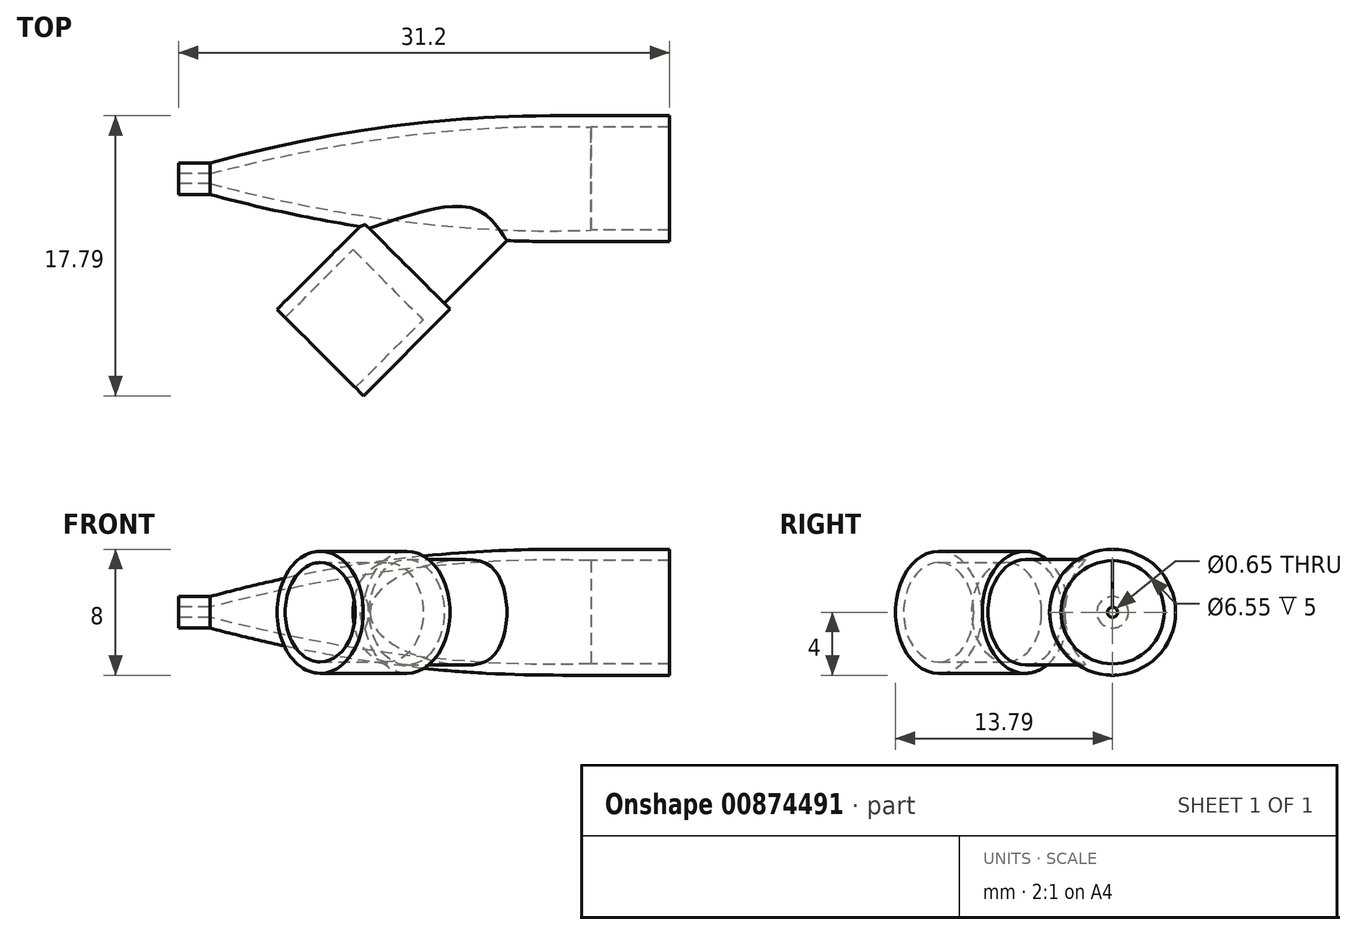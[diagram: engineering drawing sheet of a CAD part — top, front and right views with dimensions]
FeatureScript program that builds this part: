
annotation { "Feature Type Name" : "Feature", "Feature Type Description" : "" }
export const myFeature = defineFeature(function(context is Context, id is Id, definition is map)
    precondition{}
    {
        {
            var Q0;
            Q0=qCreatedBy(makeId("Front.planeOp"),FACE);
            var sketch = newSketch(context, id + "F0", { "sketchPlane" : qUnion([Q0])});
            skLineSegment(sketch, "E0.bottom", {"start": v(1, 1) * mm, "end": v(-1, 1) * mm});
            skLineSegment(sketch, "E0.top", {"start": v(1, 0.33) * mm, "end": v(-1, 0.33) * mm});
            skLineSegment(sketch, "E0.left", {"start": v(1, 1) * mm, "end": v(1, 0.33) * mm});
            skLineSegment(sketch, "E0.right", {"start": v(-1, 1) * mm, "end": v(-1, 0.32) * mm});
            skLineSegment(sketch, "E1.bottom", {"start": v(1, -0.33) * mm, "end": v(-1, -0.33) * mm, "construction": true});
            skLineSegment(sketch, "E1.top", {"start": v(1, -1) * mm, "end": v(-1, -1) * mm, "construction": true});
            skLineSegment(sketch, "E1.left", {"start": v(1, -0.33) * mm, "end": v(1, -1) * mm, "construction": true});
            skLineSegment(sketch, "E1.right", {"start": v(-1, -0.33) * mm, "end": v(-1, -1) * mm, "construction": true});
            skLineSegment(sketch, "E2", {"start": v(0, 0.33) * mm, "end": v(0, -0.33) * mm, "construction": true});
            skLineSegment(sketch, "E3.bottom", {"start": v(30.2, 3.28) * mm, "end": v(25.2, 3.28) * mm});
            skLineSegment(sketch, "E3.top", {"start": v(30.2, -4.73) * mm, "end": v(25.2, -4.72) * mm, "construction": true});
            skLineSegment(sketch, "E3.left", {"start": v(30.2, 4) * mm, "end": v(30.2, 3.28) * mm});
            skLineSegment(sketch, "E3.right", {"start": v(25.2, 4) * mm, "end": v(25.2, 3.28) * mm});
            skLineSegment(sketch, "E4.bottom", {"start": v(30.2, -4) * mm, "end": v(25.2, -4) * mm, "construction": true});
            skLineSegment(sketch, "E4.top", {"start": v(30.2, 4) * mm, "end": v(25.2, 4) * mm});
            skLineSegment(sketch, "E5.trimOffspring", {"start": v(25.2, -4) * mm, "end": v(25.2, -4.72) * mm, "construction": true});
            skLineSegment(sketch, "E6.trimOffspring", {"start": v(30.2, -4) * mm, "end": v(30.2, -4.72) * mm, "construction": true});
            skLineSegment(sketch, "E7", {"start": v(27.7, 4) * mm, "end": v(27.7, -4) * mm, "construction": true});
            skLineSegment(sketch, "E8", {"start": v(0, 0) * mm, "end": v(27.7, 0) * mm, "construction": true});
            skFitSpline(sketch, "E9", {"points": [v(25.2, 4) * mm, v(1, 1) * mm], "startDerivative": vector(-15, 0) * mm, "endDerivative": vector(-34.77, -9.32) * mm});
            skFitSpline(sketch, "E10", {"points": [v(25.2, 3.28) * mm, v(1, 0.33) * mm], "startDerivative": vector(-15, 0.45) * mm, "endDerivative": vector(-34.77, -8.93) * mm});
            skLineSegment(sketch, "E11", {"start": v(27.7, 3.28) * mm, "end": v(27.7, 0) * mm});
            skLineSegment(sketch, "E12", {"start": v(27.7, 0) * mm, "end": v(1, 0) * mm});
            skLineSegment(sketch, "E13", {"start": v(1, 0) * mm, "end": v(1, 0.33) * mm});
            skLineSegment(sketch, "E14", {"start": v(1, 1) * mm, "end": v(12.6, 4.1) * mm, "construction": true});
            skLineSegment(sketch, "E15", {"start": v(20.2, 3.28) * mm, "end": v(20.2, 4) * mm, "construction": true});
            skLineSegment(sketch, "E16", {"start": v(12.6, 3.3) * mm, "end": v(12.6, 2.63) * mm, "construction": true});
            skSolve(sketch);
        }
        {
            var Q0;
            Q0=makeQuery(id+"F0.imprint","IMPRINT",FACE,{"disambiguationData":[TD([[makeQuery(id+"F0.imprint","IMPRINT",EDGE,{"derivedFrom":sQuery(id+"F0.wireOp",EDGE,"E0.bottom")}),1.0]])]});
            var Q1;
            Q1=makeQuery(id+"F0.imprint","IMPRINT",FACE,{"disambiguationData":[TD([[makeQuery(id+"F0.imprint","IMPRINT",EDGE,{"derivedFrom":sQuery(id+"F0.wireOp",EDGE,"E0.left")}),1.0]])]});
            var Q2;
            Q2=makeQuery(id+"F0.imprint","IMPRINT",FACE,{"disambiguationData":[TD([[makeQuery(id+"F0.imprint","IMPRINT",EDGE,{"derivedFrom":sQuery(id+"F0.wireOp",EDGE,"E3.bottom")}),-1.0]])]});
            var Q3;
            Q3=sQuery(id+"F0.wireOp",EDGE,"E8");
            revolve(context, id + "F1", {"surfaceOperationType" : NewSurfaceOperationType.NEW, "entities" : qUnion([Q0, Q1, Q2]), "axis" : qUnion([Q3]), "revolveType" : RevolveType.FULL});
        }
        {
            var Q0;
            Q0=qCreatedBy(makeId("Top.planeOp"),FACE);
            var sketch = newSketch(context, id + "F2", { "sketchPlane" : qUnion([Q0])});
            skLineSegment(sketch, "E17", {"start": v(19.05, 0) * mm, "end": v(5.58, -13.47) * mm, "construction": true});
            skLineSegment(sketch, "E18", {"start": v(0, 0) * mm, "end": v(19.05, 0) * mm, "construction": true});
            skLineSegment(sketch, "E19", {"start": v(15.88, -3.18) * mm, "end": v(12.31, -6.74) * mm});
            skLineSegment(sketch, "E20", {"start": v(16.24, -8.29) * mm, "end": v(15.88, -7.92) * mm});
            skLineSegment(sketch, "E21", {"start": v(15.88, -7.92) * mm, "end": v(20.37, -3.43) * mm});
            skLineSegment(sketch, "E22", {"start": v(12.31, -6.74) * mm, "end": v(14.54, -8.96) * mm});
            skLineSegment(sketch, "E23", {"start": v(14.54, -8.96) * mm, "end": v(10.23, -13.28) * mm});
            skLineSegment(sketch, "E24", {"start": v(10.23, -13.28) * mm, "end": v(10.74, -13.79) * mm});
            skLineSegment(sketch, "E25", {"start": v(10.74, -13.79) * mm, "end": v(16.24, -8.29) * mm});
            skLineSegment(sketch, "E26", {"start": v(15.88, -3.18) * mm, "end": v(20.37, -3.43) * mm});
            skSolve(sketch);
        }
        {
            var Q0;
            Q0 = qSketchRegion(id + "F2", true);
            var Q1;
            Q1=sQuery(id+"F2.wireOp",EDGE,"E17");
            revolve(context, id + "F3", {"operationType" : NewBodyOperationType.ADD, "surfaceOperationType" : NewSurfaceOperationType.NEW, "entities" : qUnion([Q0]), "axis" : qUnion([Q1]), "revolveType" : RevolveType.FULL});
        }
        {
            var Q0;
            Q0=qCreatedBy(makeId("Front.planeOp"),FACE);
            var sketch = newSketch(context, id + "F4", { "sketchPlane" : qUnion([Q0])});
            skLineSegment(sketch, "E27.bottom", {"start": v(1, 1) * mm, "end": v(-1, 1) * mm, "construction": true});
            skLineSegment(sketch, "E27.top", {"start": v(1, 0.33) * mm, "end": v(-1, 0.33) * mm});
            skLineSegment(sketch, "E27.left", {"start": v(1, 1) * mm, "end": v(1, 0.33) * mm});
            skLineSegment(sketch, "E27.right", {"start": v(-1, 1) * mm, "end": v(-1, 0.32) * mm, "construction": true});
            skLineSegment(sketch, "E28.bottom", {"start": v(1, -0.33) * mm, "end": v(-1, -0.33) * mm, "construction": true});
            skLineSegment(sketch, "E28.top", {"start": v(1, -1) * mm, "end": v(-1, -1) * mm, "construction": true});
            skLineSegment(sketch, "E28.left", {"start": v(1, -0.33) * mm, "end": v(1, -1) * mm, "construction": true});
            skLineSegment(sketch, "E28.right", {"start": v(-1, -0.33) * mm, "end": v(-1, -1) * mm, "construction": true});
            skLineSegment(sketch, "E29", {"start": v(0, 0.33) * mm, "end": v(0, -0.33) * mm, "construction": true});
            skLineSegment(sketch, "E30.bottom", {"start": v(30.2, 3.28) * mm, "end": v(25.2, 3.28) * mm});
            skLineSegment(sketch, "E30.top", {"start": v(30.2, -4.72) * mm, "end": v(25.2, -4.72) * mm, "construction": true});
            skLineSegment(sketch, "E30.left", {"start": v(30.2, 4) * mm, "end": v(30.2, 3.28) * mm, "construction": true});
            skLineSegment(sketch, "E30.right", {"start": v(25.2, 4) * mm, "end": v(25.2, 3.28) * mm});
            skLineSegment(sketch, "E31.bottom", {"start": v(30.2, -4) * mm, "end": v(25.2, -4) * mm, "construction": true});
            skLineSegment(sketch, "E31.top", {"start": v(30.2, 4) * mm, "end": v(25.2, 4) * mm, "construction": true});
            skLineSegment(sketch, "E32.trimOffspring", {"start": v(25.2, -4) * mm, "end": v(25.2, -4.72) * mm, "construction": true});
            skLineSegment(sketch, "E33.trimOffspring", {"start": v(30.2, -4) * mm, "end": v(30.2, -4.72) * mm, "construction": true});
            skLineSegment(sketch, "E34", {"start": v(27.7, 4) * mm, "end": v(27.7, -4) * mm, "construction": true});
            skLineSegment(sketch, "E35", {"start": v(0, 0) * mm, "end": v(27.7, 0) * mm});
            skFitSpline(sketch, "E36", {"points": [v(25.2, 4) * mm, v(1, 1) * mm], "startDerivative": vector(-15, 0) * mm, "endDerivative": vector(-34.77, -9.32) * mm, "construction": true});
            skFitSpline(sketch, "E37", {"points": [v(25.2, 3.28) * mm, v(1, 0.33) * mm], "startDerivative": vector(-15, 0.45) * mm, "endDerivative": vector(-34.77, -8.93) * mm});
            skLineSegment(sketch, "E38", {"start": v(27.7, 3.28) * mm, "end": v(27.7, 0) * mm});
            skLineSegment(sketch, "E39", {"start": v(27.7, 0) * mm, "end": v(1, 0) * mm});
            skLineSegment(sketch, "E40", {"start": v(1, 0) * mm, "end": v(1, 0.33) * mm});
            skLineSegment(sketch, "E41", {"start": v(1, 1) * mm, "end": v(12.6, 4.1) * mm, "construction": true});
            skLineSegment(sketch, "E42", {"start": v(20.2, 3.28) * mm, "end": v(20.2, 4) * mm, "construction": true});
            skLineSegment(sketch, "E43", {"start": v(12.6, 3.3) * mm, "end": v(12.6, 2.63) * mm, "construction": true});
            skSolve(sketch);
        }
        {
            var Q0;
            Q0 = qSketchRegion(id + "F4", true);
            var Q1;
            Q1=sQuery(id+"F4.wireOp",EDGE,"E35");
            revolve(context, id + "F5", {"operationType" : NewBodyOperationType.REMOVE, "surfaceOperationType" : NewSurfaceOperationType.NEW, "entities" : qUnion([Q0]), "axis" : qUnion([Q1]), "revolveType" : RevolveType.FULL, "oppositeDirection" : true});
        }
    });
